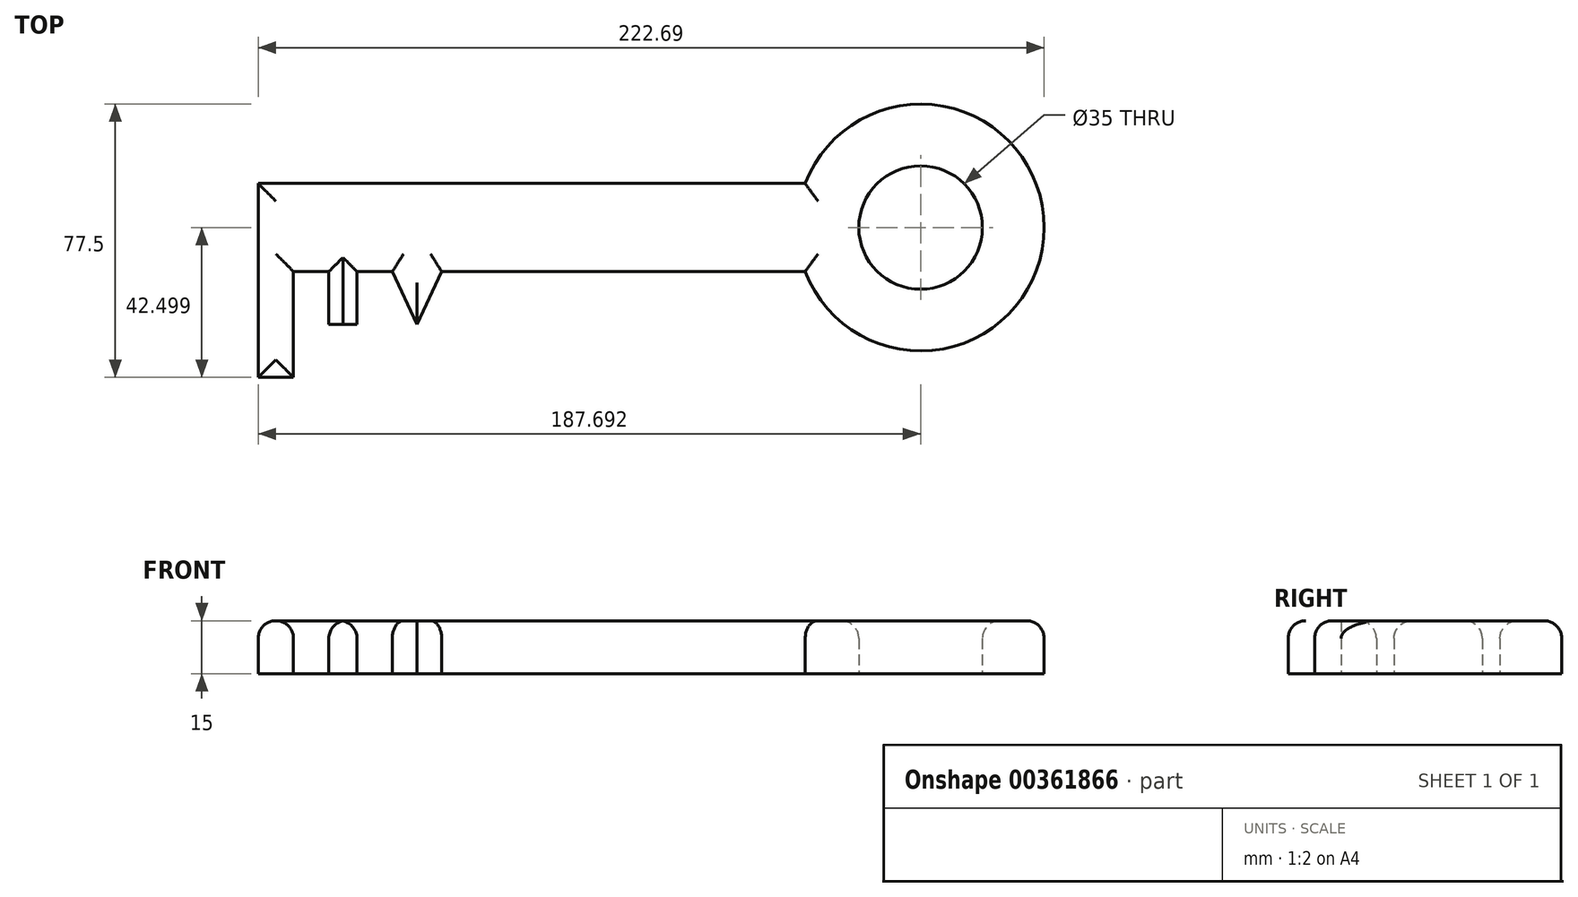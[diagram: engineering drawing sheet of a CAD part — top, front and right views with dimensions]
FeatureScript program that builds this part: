
annotation { "Feature Type Name" : "Feature", "Feature Type Description" : "" }
export const myFeature = defineFeature(function(context is Context, id is Id, definition is map)
    precondition{}
    {
        {
            var Q0;
            Q0=qCreatedBy(makeId("Top.planeOp"),FACE);
            var sketch = newSketch(context, id + "F0", { "sketchPlane" : qUnion([Q0])});
            skLineSegment(sketch, "E0.bottom", {"start": v(-52, 63.59) * mm, "end": v(103, 63.59) * mm});
            skLineSegment(sketch, "E0.top", {"start": v(-52, 38.59) * mm, "end": v(103, 38.59) * mm});
            skLineSegment(sketch, "E0.left", {"start": v(-52, 63.59) * mm, "end": v(-52, 38.59) * mm});
            skLineSegment(sketch, "E0.right", {"start": v(103, 63.59) * mm, "end": v(103, 38.59) * mm});
            skLineSegment(sketch, "E1.bottom", {"start": v(-52, 38.59) * mm, "end": v(-42, 38.59) * mm});
            skLineSegment(sketch, "E1.top", {"start": v(-52, 8.59) * mm, "end": v(-42, 8.59) * mm});
            skLineSegment(sketch, "E1.left", {"start": v(-52, 38.59) * mm, "end": v(-52, 8.59) * mm});
            skLineSegment(sketch, "E1.right", {"start": v(-42, 38.59) * mm, "end": v(-42, 8.59) * mm});
            skLineSegment(sketch, "E2.bottom", {"start": v(-32, 38.59) * mm, "end": v(-24, 38.59) * mm});
            skLineSegment(sketch, "E2.top", {"start": v(-32, 23.59) * mm, "end": v(-24, 23.59) * mm});
            skLineSegment(sketch, "E2.left", {"start": v(-32, 38.59) * mm, "end": v(-32, 23.59) * mm});
            skLineSegment(sketch, "E2.right", {"start": v(-24, 38.59) * mm, "end": v(-24, 23.59) * mm});
            skLineSegment(sketch, "E3", {"start": v(-14, 38.59) * mm, "end": v(-7, 23.59) * mm});
            skLineSegment(sketch, "E4", {"start": v(-7, 23.59) * mm, "end": v(0, 38.59) * mm});
            skLineSegment(sketch, "E5", {"start": v(0, 38.59) * mm, "end": v(-14, 38.59) * mm});
            skArc(sketch, "E6", {"start": v(103, 38.59) * mm, "mid": v(170.7, 51.09) * mm, "end": v(103, 63.59) * mm});
            skCircle(sketch, "E7", {"center": v(135.7, 51.09) * mm, "radius": 17.5 * mm});
            skLineSegment(sketch, "E8", {"start": v(-52, 51.09) * mm, "end": v(135.7, 51.09) * mm, "construction": true});
            skSolve(sketch);
        }
        {
            var Q0;
            Q0 = qSketchRegion(id + "F0", true);
            extrude(context, id + "F1", {"entities" : qUnion([Q0]), "depth" : 15 * mm});
        }
        {
            var Q0;
            Q0=makeQuery(id+"F1.opExtrude","CAP_EDGE",EDGE,{"disambiguationData":[OSD([sQuery(id+"F0.wireOp",EDGE,"E0.bottom")])],"isStart":false});
            var Q1;
            Q1=makeQuery(id+"F1.opExtrude","CAP_EDGE",EDGE,{"disambiguationData":[OSD([sQuery(id+"F0.wireOp",EDGE,"E0.left"),sQuery(id+"F0.wireOp",EDGE,"E1.left")])],"isStart":false});
            var Q2;
            Q2=makeQuery(id+"F1.opExtrude","CAP_EDGE",EDGE,{"disambiguationData":[OSD([sQuery(id+"F0.wireOp",EDGE,"E1.right")])],"isStart":false});
            var Q3;
            Q3=makeQuery(id+"F1.opExtrude","CAP_EDGE",EDGE,{"disambiguationData":[OSD([sQuery(id+"F0.wireOp",EDGE,"E1.top")])],"isStart":false});
            var Q4;
            {var subQ0=sQuery(id+"F0.wireOp",EDGE,"E0.top");Q4=makeQuery(id+"F1.opExtrude","CAP_EDGE",EDGE,{"disambiguationData":[OSD([subQ0]),TDD([makeQuery(id+"F0.imprint","IMPRINT",EDGE,{"disambiguationData":[TD([[makeQuery(id+"F0.imprint","INTERSECT",VERTEX,{"derivedFrom":[subQ0,sQuery(id+"F0.wireOp",EDGE,"E1.bottom"),sQuery(id+"F0.wireOp",EDGE,"E1.right")]}),-1.0]])],"derivedFrom":subQ0})])],"isStart":false});}
            var Q5;
            Q5=makeQuery(id+"F1.opExtrude","CAP_EDGE",EDGE,{"disambiguationData":[OSD([sQuery(id+"F0.wireOp",EDGE,"E2.left")])],"isStart":false});
            var Q6;
            {var subQ0=sQuery(id+"F0.wireOp",EDGE,"E0.top");Q6=makeQuery(id+"F1.opExtrude","CAP_EDGE",EDGE,{"disambiguationData":[OSD([subQ0]),TDD([makeQuery(id+"F0.imprint","IMPRINT",EDGE,{"disambiguationData":[TD([[makeQuery(id+"F0.imprint","INTERSECT",VERTEX,{"derivedFrom":[subQ0,sQuery(id+"F0.wireOp",EDGE,"E2.bottom"),sQuery(id+"F0.wireOp",EDGE,"E2.right")]}),-1.0]])],"derivedFrom":subQ0})])],"isStart":false});}
            var Q7;
            Q7=makeQuery(id+"F1.opExtrude","CAP_EDGE",EDGE,{"disambiguationData":[OSD([sQuery(id+"F0.wireOp",EDGE,"E2.right")])],"isStart":false});
            var Q8;
            Q8=makeQuery(id+"F1.opExtrude","CAP_EDGE",EDGE,{"disambiguationData":[OSD([sQuery(id+"F0.wireOp",EDGE,"E3")])],"isStart":false});
            var Q9;
            {var subQ0=sQuery(id+"F0.wireOp",EDGE,"E0.top");Q9=makeQuery(id+"F1.opExtrude","CAP_EDGE",EDGE,{"disambiguationData":[OSD([subQ0]),TDD([makeQuery(id+"F0.imprint","IMPRINT",EDGE,{"disambiguationData":[TD([[makeQuery(id+"F0.imprint","INTERSECT",VERTEX,{"derivedFrom":[subQ0,sQuery(id+"F0.wireOp",EDGE,"E0.right"),sQuery(id+"F0.wireOp",EDGE,"E6")]}),1.0]])],"derivedFrom":subQ0})])],"isStart":false});}
            var Q10;
            Q10=makeQuery(id+"F1.opExtrude","CAP_EDGE",EDGE,{"disambiguationData":[OSD([sQuery(id+"F0.wireOp",EDGE,"E4")])],"isStart":false});
            var Q11;
            Q11=makeQuery(id+"F1.opExtrude","CAP_EDGE",EDGE,{"disambiguationData":[OSD([sQuery(id+"F0.wireOp",EDGE,"E6")])],"isStart":false});
            var Q12;
            Q12=makeQuery(id+"F1.opExtrude","CAP_EDGE",EDGE,{"disambiguationData":[OSD([sQuery(id+"F0.wireOp",EDGE,"E7")])],"isStart":false});
            fillet(context, id + "F2", {"entities" : qUnion([Q0, Q1, Q2, Q3, Q4, Q5, Q6, Q7, Q8, Q9, Q10, Q11, Q12]), "radius" : 5 * mm, "tangentPropagation" : true, "allowEdgeOverflow" : false});
        }
    });
